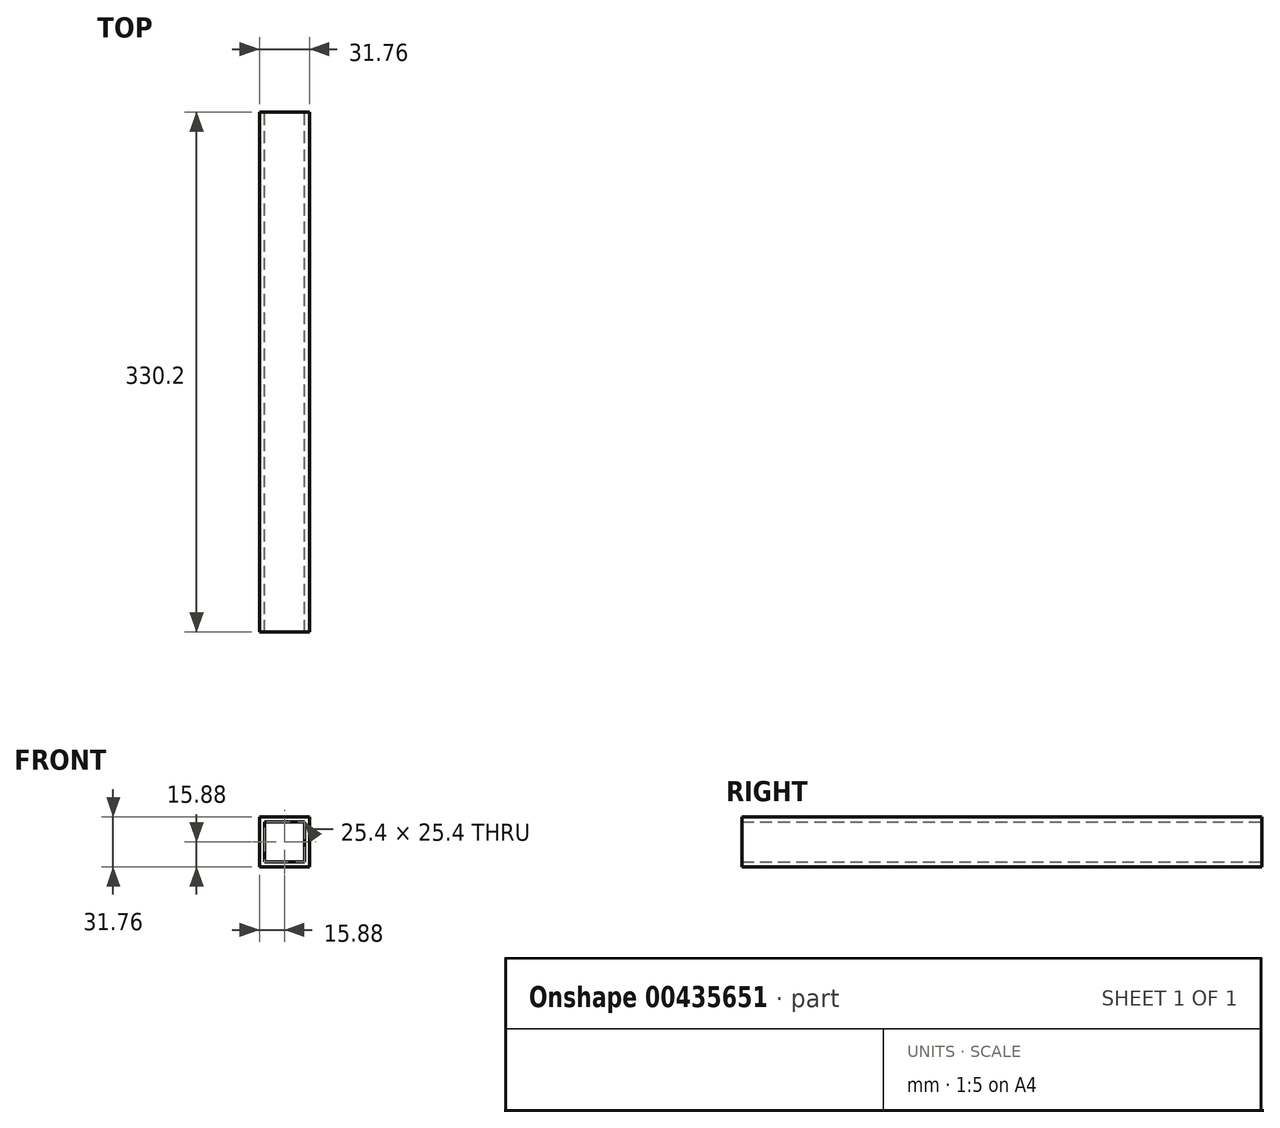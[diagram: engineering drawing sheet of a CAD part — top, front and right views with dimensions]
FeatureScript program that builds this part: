
annotation { "Feature Type Name" : "Feature", "Feature Type Description" : "" }
export const myFeature = defineFeature(function(context is Context, id is Id, definition is map)
    precondition{}
    {
        {
            var Q0;
            Q0=qCreatedBy(makeId("Front.planeOp"),FACE);
            var sketch = newSketch(context, id + "F0", { "sketchPlane" : qUnion([Q0])});
            skLineSegment(sketch, "E0.bottom", {"start": v(12.7, -12.7) * mm, "end": v(-12.7, -12.7) * mm});
            skLineSegment(sketch, "E0.top", {"start": v(12.7, 12.7) * mm, "end": v(-12.7, 12.7) * mm});
            skLineSegment(sketch, "E0.left", {"start": v(12.7, -12.7) * mm, "end": v(12.7, 12.7) * mm});
            skLineSegment(sketch, "E0.right", {"start": v(-12.7, -12.7) * mm, "end": v(-12.7, 12.7) * mm});
            skPoint(sketch, "E0.middle", {"position": v(0, 0) * mm});
            skLineSegment(sketch, "E1.0", {"start": v(15.88, 15.88) * mm, "end": v(-15.87, 15.87) * mm});
            skLineSegment(sketch, "E1.1", {"start": v(15.88, -15.87) * mm, "end": v(15.88, 15.88) * mm});
            skLineSegment(sketch, "E1.2", {"start": v(15.88, -15.87) * mm, "end": v(-15.87, -15.88) * mm});
            skLineSegment(sketch, "E1.3", {"start": v(-15.87, -15.88) * mm, "end": v(-15.87, 15.87) * mm});
            skSolve(sketch);
        }
        {
            var Q0;
            Q0 = qSketchRegion(id + "F0", true);
            extrude(context, id + "F1", {"entities" : qUnion([Q0]), "depth" : 330.2 * mm});
        }
    });
